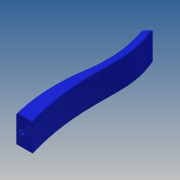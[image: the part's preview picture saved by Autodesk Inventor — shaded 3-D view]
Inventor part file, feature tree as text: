
AUTODESK INVENTOR PART (.ipt)
format: ipt  version: 2014 (Build 180170000, 170)  size: 149,504 bytes
history: native  units: mm
features: extrude x2, sketch x2, fillet x1
ambient origin geometry x8: Origin, YZ Plane, XZ Plane, XY Plane, X Axis, Y Axis, Z Axis, Center Point
bodies: Body1 (feature_tree)
feature tree (5):
  extrude  "Extrusion3"  Depth=450.0mm
  fillet  "Rundung1"  Radius=670.0mm
  extrude  "Extrusion4"  Depth=10.0mm
  sketch  "Skizze3"  dims[d5=800.0mm d8=450.0mm d9=670.0mm]
  sketch  "Skizze8"  dims[d10=30.0mm d11=40.0mm d12=30.0mm d14=50.0mm d16=130.0mm d18=90.0mm d19=740.0mm d21=90.0mm d22=230.0mm d23=140.0mm d26=100.0mm d28=730.0mm d34=160.0mm d35=30.0mm d36=770.0mm d38=100.0mm d51=323.428015mm d52=250.0mm d53=2170.0mm d59=150.0mm d60=0.0mm d61=10.0mm d62=25.0mm d63=70.0mm d64=30.0mm d65=100.0mm d66=0.0mm]
